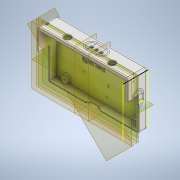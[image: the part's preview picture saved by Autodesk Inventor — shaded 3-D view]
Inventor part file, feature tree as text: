
AUTODESK INVENTOR PART (.ipt)
format: ipt  version: 2021.1 (Build 251245000, 245)  size: 1,233,920 bytes
history: native  units: mm
features: other x11, plane x8, fillet x6, delete_face x5, sketch x5, draft x3, direct_edit x2, hole x2, move_body x2, extrude x1, revolve x1, reference x1, projected_geometry x1
ambient origin geometry x8: Origin, YZ Plane, XZ Plane, XY Plane, X Axis, Y Axis, Z Axis, Center Point
bodies: Solid1 (feature_tree)
feature tree (48):
  other  "improved_case.ipt"
  plane  "Work Plane1"
  plane  "Work Plane2"
  plane  "Work Plane3"
  other  "Lip2"
  other  "Lip3"
  other  "Lip4"
  other  "Lip5"
  plane  "Work Plane4"
  plane  "Work Plane5"
  other  "Lip6"
  delete_face  "Delete Face1"
  delete_face  "Delete Face2"
  delete_face  "Delete Face3"
  fillet  "Fillet1"  Radius=10.0mm
  draft  "FaceDraft1"
  draft  "FaceDraft2"
  delete_face  "Delete Face4"
  delete_face  "Delete Face5"
  fillet  "Fillet2"  Radius=1.0mm
  sketch  "Sketch2"  dims[d7=1.0mm d8=0.9mm d9=0.0mm d10=0.0mm d11=0.872665mm d12=0.0mm]
  plane  "Work Plane6"
  extrude  "Extrusion1"  Depth=2.0mm
  plane  "Work Plane7"
  revolve  "Revolution1"  [1 undecoded]
  fillet  "Fillet3"  Radius=2.0mm
  draft  "FaceDraft3"
  fillet  "Fillet4"  Radius=2.0mm
  plane  "Work Plane8"
  direct_edit  "Direct Edit2"
  direct_edit  "Direct Edit3"
  fillet  "Fillet5"  Radius=6.0mm
  fillet  "Fillet6"  Radius=3.0mm
  hole  "Hole1"  [1 undecoded]
  hole  "Hole2"  [1 undecoded]
  other  "Solid2::improved_case.ipt"
  other  "TaggingFeature1"
  reference  "Reference1"
  sketch  "Sketch3"  dims[d13=1.0mm d14=0.9mm d15=0.0mm d16=0.0mm d17=0.872665mm d18=0.0mm]
  sketch  "Sketch4"  dims[d19=1.0mm d20=0.9mm d21=0.0mm d22=0.0mm d23=0.872665mm d24=0.0mm d25=1.0mm d26=0.9mm d27=0.0mm d28=0.0mm d29=0.872665mm d30=0.0mm]
  projected_geometry  "Projected Loop4"
  sketch  "Sketch5"  dims[d31=1.0mm d32=0.9mm d33=0.0mm d34=0.0mm d35=0.872665mm d36=0.0mm d40=1.0mm]
  sketch  "Sketch6"  dims[d41=45.0deg d42=3.490659mm d43=1.0mm d44=2.0mm d45=2.0mm d46=6.0mm d47=0.0mm d48=3.0mm d49=1.0mm d52=90.0deg d53=0.5mm d54=45.0deg d55=0.5mm d56=-13.0mm d57=0.0mm d58=0.0mm d59=-1.5mm d60=0.0mm d61=0.0mm d62=-1.0mm d63=3.0mm d64=0.5mm d65=1.0mm d66=10.0mm d67=5.1mm d68=12.1mm d69=18.5mm d70=1.0mm d71=6.0mm d72=2.0mm d73=2.0mm d74=90.0deg d75=8.0mm d76=20.594885mm d77=34.6mm d78=34.6mm d79=1.5mm d80=13.0mm d81=16.7mm d82=14.0mm d83=40.8mm d84=10.0mm d85=1.0mm d86=6.0mm d87=2.0mm d88=2.0mm d89=90.0deg d90=8.0mm d91=20.594885mm]
  other  "<userpath>\OneDrive\Projects\RepRap\NanoVNA v2 case\improved_case.iam"
  other  "improved_case.iam"
  other  "improved_top:1"
  move_body  "Move2"
  move_body  "Move3"
note: 3 required parameter values undecoded (feature->parameter linkage not recoverable at this tier; creation-order binding heuristic only, values carry confidence <= 0.55)